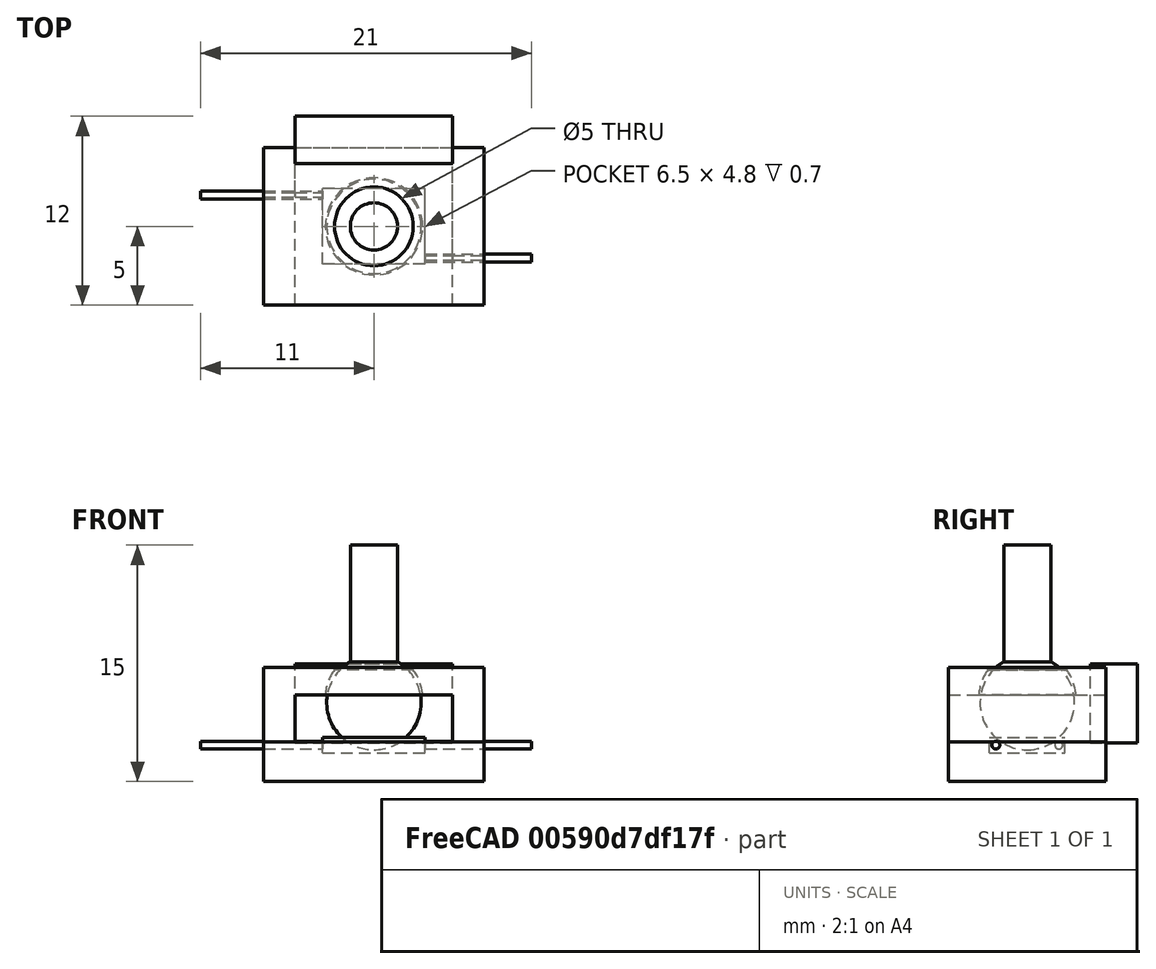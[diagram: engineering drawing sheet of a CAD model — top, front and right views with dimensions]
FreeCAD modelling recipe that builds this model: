
FCSTD DOCUMENT  (FreeCAD 0.16R6710 (Git))
Label: Feet sensors0.1
License: All rights reserved
LicenseURL: http://en.wikipedia.org/wiki/All_rights_reserved
objects: Part::Box×7, Part::Cylinder×6, Part::Fuse×6, Part::Cut×5, Part::Sphere×2, Part::MultiCommon×1
note: 27 computed .brp shape members not serialized (recipe doc carries the construction recipe); baked Part::Feature solids carry a one-line shape summary decoded from their .brp

FEATURE [Part::Sphere] Sphere
  Angle1 = -90
  Angle2 = 90
  Angle3 = 360
  Radius = 3
FEATURE [Part::Cylinder] Cylinder
  Angle = 360
  Height = 10
  Radius = 1.5
FEATURE [Part::Box] Box  label="Cube"
  Height = 1
  Length = 6.5
  Placement = pos=(-3.25,-2.4,-4.2) rot=(0,0,1;0rad)
  Width = 4.8
FEATURE [Part::Cylinder] Cylinder001
  Angle = 360
  Height = 10
  Placement = pos=(-11,2,-3.7) rot=(0,1,0;1.5708rad)
  Radius = 0.25
FEATURE [Part::Cylinder] Cylinder002
  Angle = 360
  Height = 10
  Placement = pos=(0,-2,-3.7) rot=(0,1,0;1.5708rad)
  Radius = 0.25
FEATURE [Part::Box] Box001  label="Cube001"
  Height = 7.25
  Length = 14
  Placement = pos=(-7,-5,-6) rot=(0,0,1;0rad)
  Width = 10
FEATURE [Part::Box] Box002  label="Cube002"
  Height = 1
  Length = 6.5
  Placement = pos=(-3.25,-2.4,-4.2) rot=(0,0,1;0rad)
  Width = 4.8
FEATURE [Part::Cylinder] Cylinder003
  Angle = 360
  Height = 10
  Placement = pos=(-11,2,-3.7) rot=(0,1,0;1.5708rad)
  Radius = 0.25
FEATURE [Part::Cylinder] Cylinder004
  Angle = 360
  Height = 10
  Placement = pos=(0,-2,-3.7) rot=(0,1,0;1.5708rad)
  Radius = 0.25
FEATURE [Part::Fuse] Fusion
  Base = -> Cylinder003
  Tool = -> Cylinder004
FEATURE [Part::Fuse] Fusion001
  Base = -> Box002
  Tool = -> Fusion
FEATURE [Part::Box] Box003  label="Cube003"
  Height = 3
  Length = 10
  Placement = pos=(-5,-6,-3.5) rot=(0,0,1;0rad)
  Width = 12
FEATURE [Part::Cut] Cut
  Base = -> Box001
  Tool = -> Box003
FEATURE [Part::Cut] Cut001
  Base = -> Cut
  Tool = -> Fusion001
FEATURE [Part::Fuse] Fusion002
  Base = -> Cylinder001
  Tool = -> Cylinder002
FEATURE [Part::Fuse] Fusion003  label="Switch"
  Base = -> Box
  Tool = -> Fusion002
FEATURE [Part::Box] Box004  label="Cube004"
  Height = 5
  Length = 10
  Placement = pos=(-5,4,-3.55) rot=(0,0,1;0rad)
  Width = 3
FEATURE [Part::Sphere] Sphere001
  Angle1 = -90
  Angle2 = 90
  Angle3 = 360
  Placement = pos=(0,0,-0.75) rot=(0,0,1;0rad)
  Radius = 3.1
FEATURE [Part::Cylinder] Cylinder005
  Angle = 360
  Height = 10
  Placement = pos=(0,0,0.5) rot=(0,0,1;0rad)
  Radius = 2.5
FEATURE [Part::Fuse] Fusion004
  Base = -> Sphere001
  Tool = -> Cylinder005
FEATURE [Part::Cut] Cut002
  Base = -> Cut001
  Tool = -> Fusion004
FEATURE [Part::Fuse] Fusion005  label="Ball and Screw"
  Base = -> Sphere
  Placement = pos=(0,0,-1) rot=(0,0,1;0rad)
  Tool = -> Cylinder
FEATURE [Part::Cut] Cut003
  Base = -> Cut001
  Tool = -> Fusion004
FEATURE [Part::Box] Box005  label="Cube005"
  Height = 8
  Length = 21
  Placement = pos=(-9,-7,-3.5) rot=(0,0,1;0rad)
  Width = 17
FEATURE [Part::Box] Box006  label="Cube006"
  Height = 12
  Length = 21
  Placement = pos=(-9,-7,-3.5) rot=(0,0,1;0rad)
  Width = 17
FEATURE [Part::Cut] Cut004  label="Bottom Switch holder"
  Base = -> Cut003
  Tool = -> Box005
FEATURE [Part::MultiCommon] Common  label="Ball and screw holder"
  Shapes = -> [Cut002,Box006]
